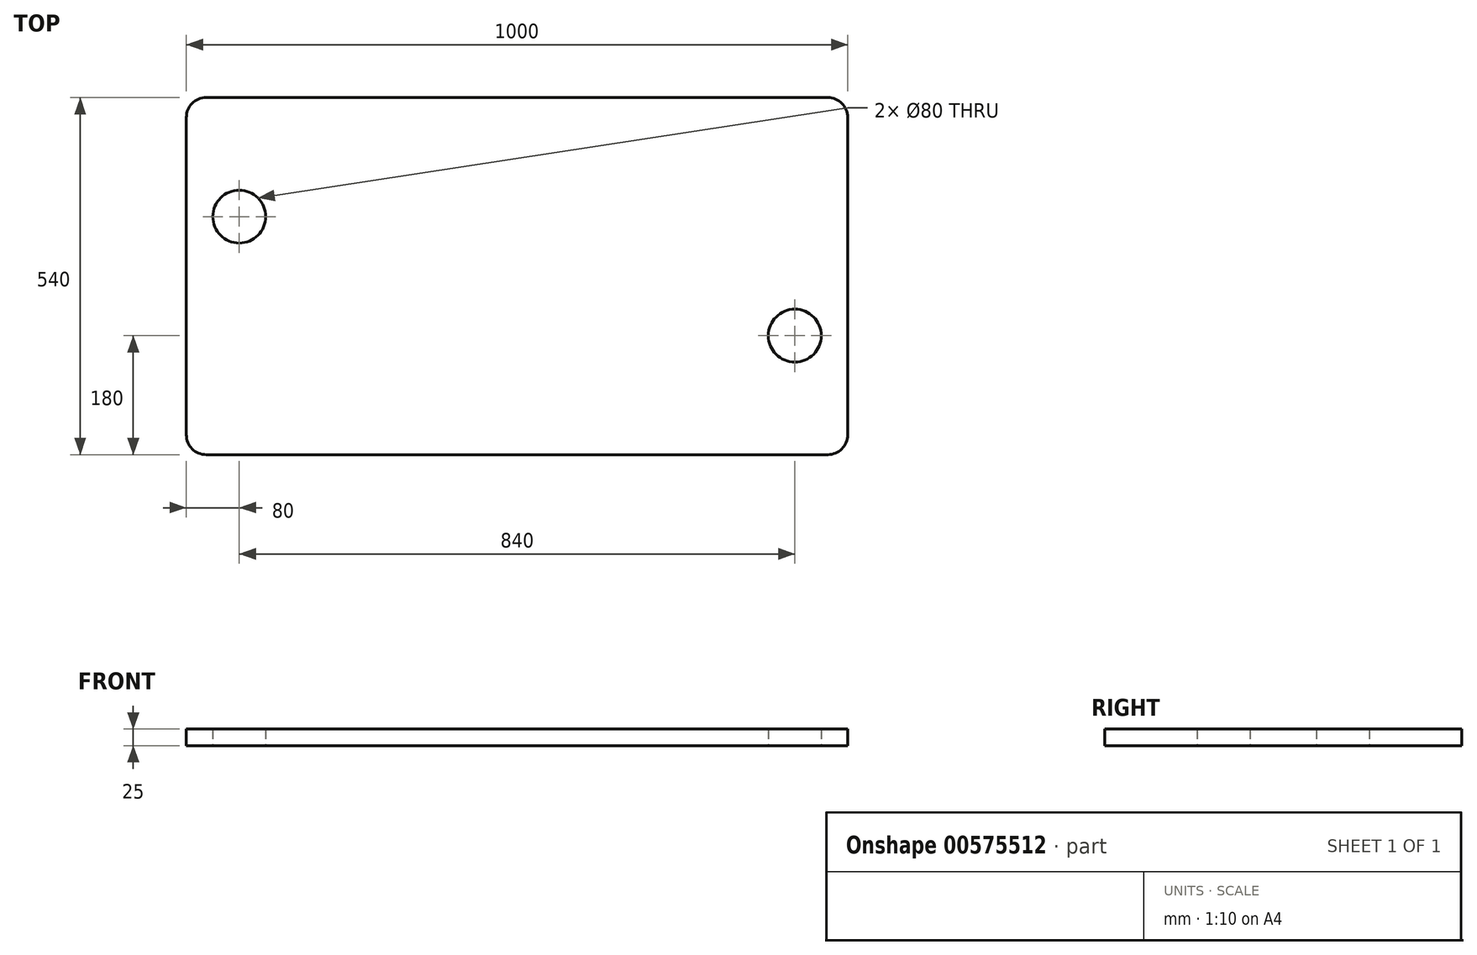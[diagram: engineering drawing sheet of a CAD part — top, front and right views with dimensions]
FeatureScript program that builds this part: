
annotation { "Feature Type Name" : "Feature", "Feature Type Description" : "" }
export const myFeature = defineFeature(function(context is Context, id is Id, definition is map)
    precondition{}
    {
        {
            var Q0;
            Q0=qCreatedBy(makeId("Top.planeOp"),FACE);
            var sketch = newSketch(context, id + "F0", { "sketchPlane" : qUnion([Q0])});
            skLineSegment(sketch, "E0.bottom", {"start": v(470, 270) * mm, "end": v(-470, 270) * mm});
            skLineSegment(sketch, "E0.top", {"start": v(470, -270) * mm, "end": v(-470, -270) * mm});
            skLineSegment(sketch, "E0.left", {"start": v(500, 240) * mm, "end": v(500, -240) * mm});
            skLineSegment(sketch, "E0.right", {"start": v(-500, 240) * mm, "end": v(-500, -240) * mm});
            skPoint(sketch, "E0.middle", {"position": v(0, 0) * mm});
            skLineSegment(sketch, "E1.bottom", {"start": v(500, 170) * mm, "end": v(-500, 170) * mm});
            skLineSegment(sketch, "E1.top", {"start": v(500, -170) * mm, "end": v(-500, -170) * mm});
            skLineSegment(sketch, "E1.left", {"start": v(500, 170) * mm, "end": v(500, -170) * mm});
            skLineSegment(sketch, "E1.right", {"start": v(-500, 170) * mm, "end": v(-500, -170) * mm});
            skPoint(sketch, "E2.visualSharp", {"position": v(-500, 270) * mm});
            skArc(sketch, "E2.filletArc", {"start": v(-470, 270) * mm, "mid": v(-491.21, 261.21) * mm, "end": v(-500, 240) * mm});
            skPoint(sketch, "E3.visualSharp", {"position": v(500, 270) * mm});
            skArc(sketch, "E3.filletArc", {"start": v(500, 240) * mm, "mid": v(491.21, 261.21) * mm, "end": v(470, 270) * mm});
            skPoint(sketch, "E4.visualSharp", {"position": v(-500, -270) * mm});
            skArc(sketch, "E4.filletArc", {"start": v(-500, -240) * mm, "mid": v(-491.21, -261.21) * mm, "end": v(-470, -270) * mm});
            skPoint(sketch, "E5.visualSharp", {"position": v(500, -270) * mm});
            skArc(sketch, "E5.filletArc", {"start": v(470, -270) * mm, "mid": v(491.21, -261.21) * mm, "end": v(500, -240) * mm});
            skCircle(sketch, "E6", {"center": v(-420, 90) * mm, "radius": 40 * mm});
            skCircle(sketch, "E7", {"center": v(420, -90) * mm, "radius": 40 * mm});
            skSolve(sketch);
        }
        {
            var Q0;
            Q0=makeQuery(id+"F0.imprint","IMPRINT",FACE,{"disambiguationData":[TD([[makeQuery(id+"F0.imprint","IMPRINT",EDGE,{"derivedFrom":sQuery(id+"F0.wireOp",EDGE,"E0.bottom")}),1.0]])]});
            var Q1;
            Q1=makeQuery(id+"F0.imprint","IMPRINT",FACE,{"disambiguationData":[TD([[makeQuery(id+"F0.imprint","IMPRINT",EDGE,{"derivedFrom":sQuery(id+"F0.wireOp",EDGE,"E0.top")}),-1.0]])]});
            var Q2;
            {var subQ1=sQuery(id+"F0.wireOp",EDGE,"E1.bottom");Q2=makeQuery(id+"F0.imprint","IMPRINT",FACE,{"disambiguationData":[TD([[makeQuery(id+"F0.imprint","IMPRINT",EDGE,{"derivedFrom":subQ1}),1.0]])]});}
            extrude(context, id + "F1", {"entities" : qUnion([Q0, Q1, Q2]), "depth" : 25 * mm, "offsetDistance" : 25 * mm});
        }
    });
